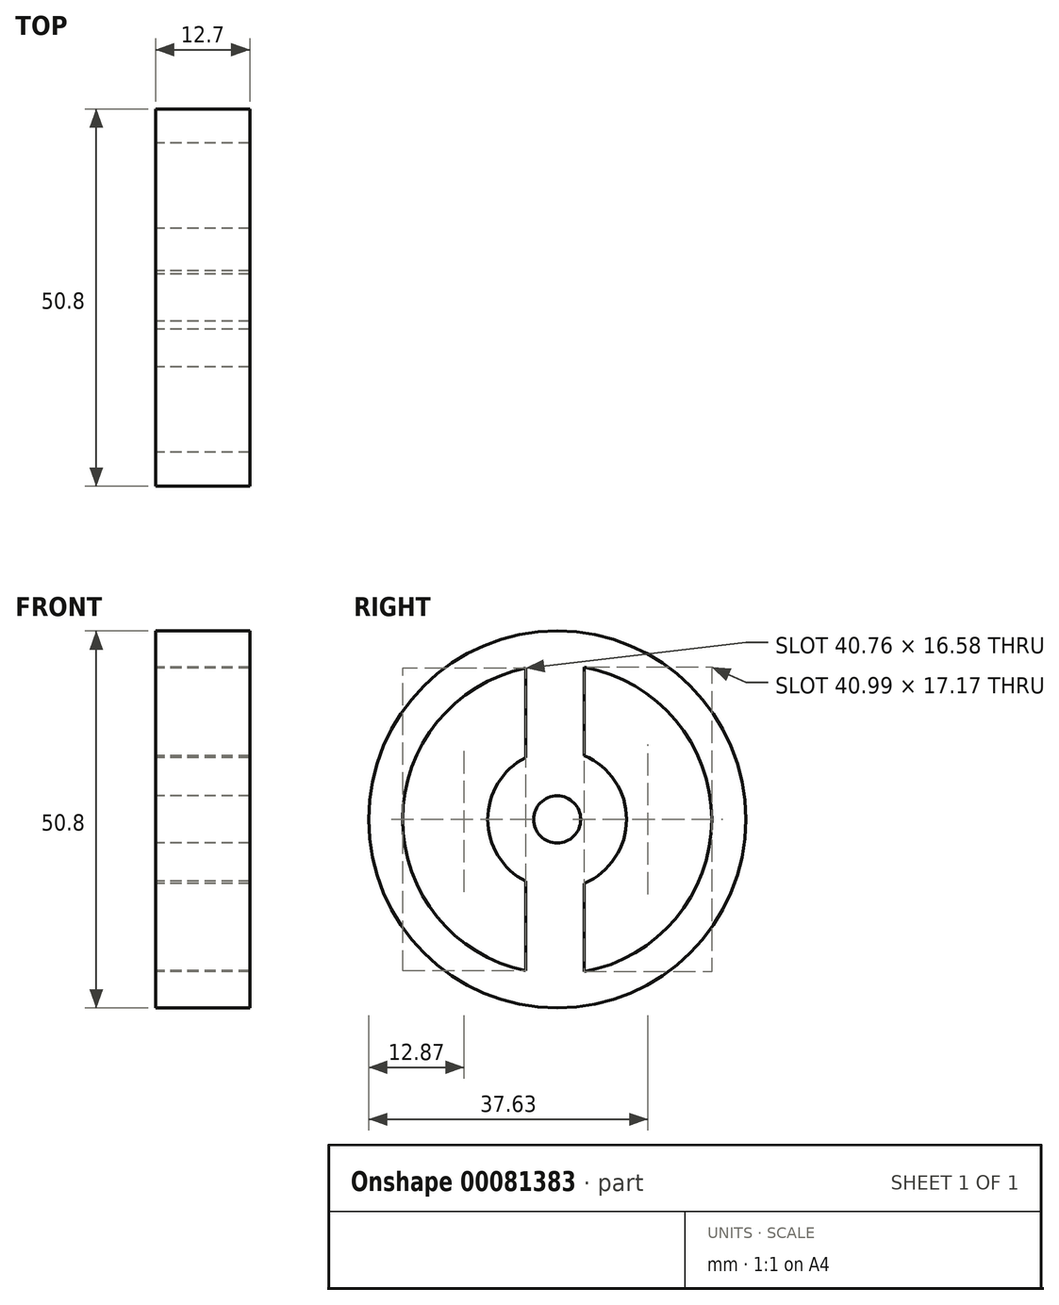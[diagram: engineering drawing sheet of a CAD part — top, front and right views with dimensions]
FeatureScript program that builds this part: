
annotation { "Feature Type Name" : "Feature", "Feature Type Description" : "" }
export const myFeature = defineFeature(function(context is Context, id is Id, definition is map)
    precondition{}
    {
        {
            var Q0;
            Q0=qCreatedBy(makeId("Right.planeOp"),FACE);
            var sketch = newSketch(context, id + "F0", { "sketchPlane" : qUnion([Q0])});
            skCircle(sketch, "E0", {"center": v(0, 0) * mm, "radius": 25.4 * mm});
            skArc(sketch, "E1", {"start": v(-4.24, 20.38) * mm, "mid": v(-20.82, 0) * mm, "end": v(-4.24, -20.38) * mm});
            skArc(sketch, "E2", {"start": v(-4.24, 8.33) * mm, "mid": v(-9.35, 0) * mm, "end": v(-4.24, -8.33) * mm});
            skCircle(sketch, "E3", {"center": v(0, 0) * mm, "radius": 3.18 * mm});
            skLineSegment(sketch, "E4", {"start": v(3.64, 8.61) * mm, "end": v(3.64, 20.5) * mm});
            skLineSegment(sketch, "E5", {"start": v(-4.24, 8.33) * mm, "end": v(-4.24, 20.38) * mm});
            skLineSegment(sketch, "E6", {"start": v(-4.24, -8.33) * mm, "end": v(-4.24, -20.38) * mm});
            skLineSegment(sketch, "E7", {"start": v(3.64, -8.61) * mm, "end": v(3.64, -20.5) * mm});
            skPoint(sketch, "E7.startSnap0", {"position": v(3.64, 14.55) * mm});
            skArc(sketch, "E8.trimOffspring", {"start": v(3.64, -8.61) * mm, "mid": v(9.35, 0) * mm, "end": v(3.64, 8.61) * mm});
            skArc(sketch, "E9.trimOffspring", {"start": v(3.64, -20.5) * mm, "mid": v(20.82, 0) * mm, "end": v(3.64, 20.5) * mm});
            skSolve(sketch);
        }
        {
            var Q0;
            Q0 = qSketchRegion(id + "F0", true);
            extrude(context, id + "F1", {"entities" : qUnion([Q0]), "depth" : 12.7 * mm});
        }
    });
